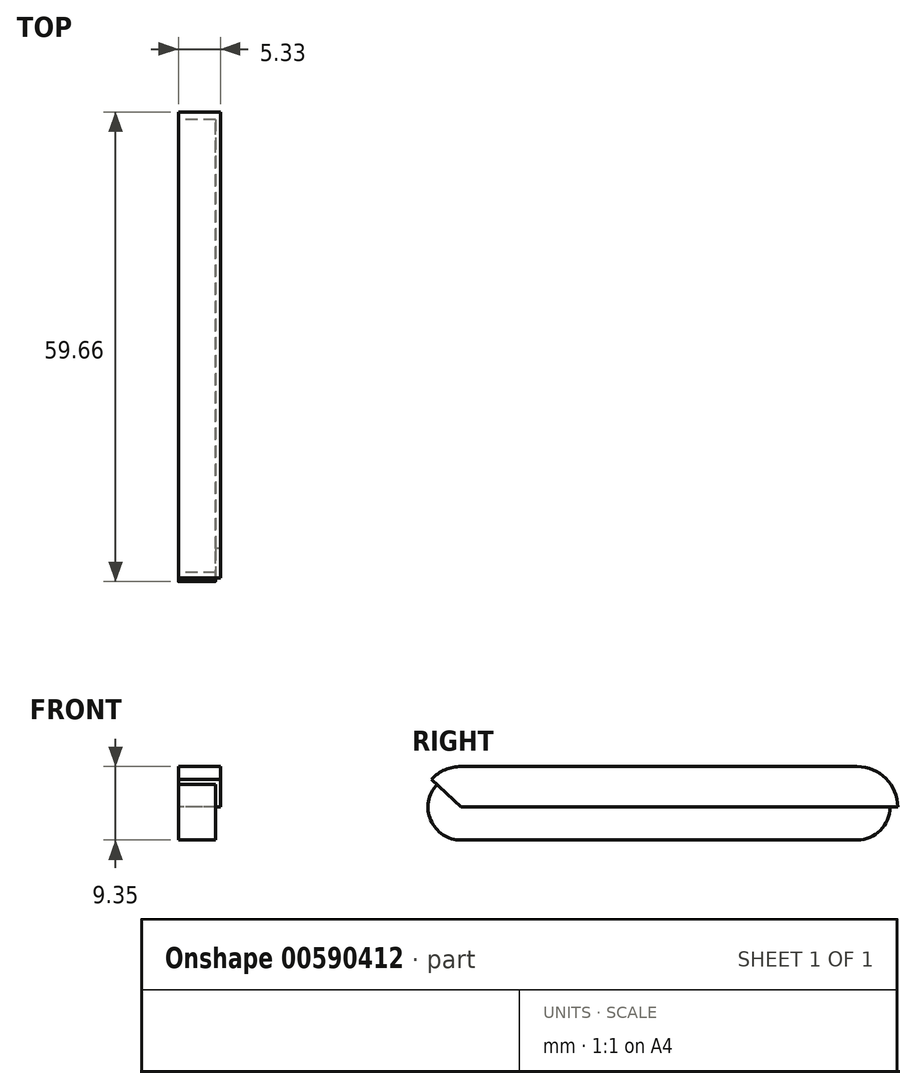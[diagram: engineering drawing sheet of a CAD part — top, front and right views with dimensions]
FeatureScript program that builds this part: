
annotation { "Feature Type Name" : "Feature", "Feature Type Description" : "" }
export const myFeature = defineFeature(function(context is Context, id is Id, definition is map)
    precondition{}
    {
        {
            var Q0;
            Q0=qCreatedBy(makeId("Right.planeOp"),FACE);
            var sketch = newSketch(context, id + "F0", { "sketchPlane" : qUnion([Q0])});
            skLineSegment(sketch, "E0", {"start": v(0, 0) * mm, "end": v(-50.32, 0) * mm});
            skLineSegment(sketch, "E1", {"start": v(0, 0) * mm, "end": v(0, 5.16) * mm});
            skLineSegment(sketch, "E2", {"start": v(0, 5.16) * mm, "end": v(-50.32, 5.16) * mm});
            skLineSegment(sketch, "E3", {"start": v(-50.32, 5.16) * mm, "end": v(-50.32, 0) * mm});
            skArc(sketch, "E4", {"start": v(0, 5.16) * mm, "mid": v(3.65, 3.65) * mm, "end": v(5.16, 0) * mm});
            skLineSegment(sketch, "E5", {"start": v(5.16, 0) * mm, "end": v(0, 0) * mm});
            skArc(sketch, "E6", {"start": v(-50.32, 5.16) * mm, "mid": v(-52.35, 4.74) * mm, "end": v(-54.06, 3.55) * mm});
            skLineSegment(sketch, "E7", {"start": v(-54.06, 3.55) * mm, "end": v(-50.32, 0) * mm});
            skSolve(sketch);
        }
        {
            var Q0;
            Q0=makeQuery(id+"F0.imprint","IMPRINT",FACE,{"disambiguationData":[TD([[makeQuery(id+"F0.imprint","IMPRINT",EDGE,{"derivedFrom":sQuery(id+"F0.wireOp",EDGE,"E0")}),-1.0]])]});
            var Q1;
            Q1=makeQuery(id+"F0.imprint","IMPRINT",FACE,{"disambiguationData":[TD([[makeQuery(id+"F0.imprint","IMPRINT",EDGE,{"derivedFrom":sQuery(id+"F0.wireOp",EDGE,"E3")}),-1.0]])]});
            var Q2;
            Q2=makeQuery(id+"F0.imprint","IMPRINT",FACE,{"disambiguationData":[TD([[makeQuery(id+"F0.imprint","IMPRINT",EDGE,{"derivedFrom":sQuery(id+"F0.wireOp",EDGE,"E1")}),-1.0]])]});
            var Q3;
            Q3=sQuery(id+"F0.wireOp",EDGE,"E2");
            var Q4;
            Q4=sQuery(id+"F0.wireOp",EDGE,"E6");
            var Q5;
            Q5=sQuery(id+"F0.wireOp",EDGE,"E7");
            var Q6;
            Q6=sQuery(id+"F0.wireOp",EDGE,"E0");
            var Q7;
            Q7=sQuery(id+"F0.wireOp",EDGE,"E4");
            var Q8;
            Q8=sQuery(id+"F0.wireOp",EDGE,"E5");
            extrude(context, id + "F1", {"entities" : qUnion([Q0, Q1, Q2]), "surfaceEntities" : qUnion([Q3, Q4, Q5, Q6, Q7, Q8]), "depth" : 5.33 * mm, "offsetDistance" : 25.4 * mm});
        }
        {
            var Q0;
            Q0=qCreatedBy(makeId("Right.planeOp"),FACE);
            var sketch = newSketch(context, id + "F2", { "sketchPlane" : qUnion([Q0])});
            skLineSegment(sketch, "E8", {"start": v(0, 0) * mm, "end": v(0, -4.19) * mm});
            skLineSegment(sketch, "E9", {"start": v(0, 0) * mm, "end": v(-50.32, 0) * mm});
            skLineSegment(sketch, "E10", {"start": v(-50.32, 0) * mm, "end": v(-50.32, -4.19) * mm});
            skLineSegment(sketch, "E11", {"start": v(-50.32, -4.19) * mm, "end": v(0, -4.19) * mm});
            skArc(sketch, "E12", {"start": v(-50.32, -4.19) * mm, "mid": v(-54.17, -1.65) * mm, "end": v(-53.35, 2.89) * mm});
            skLineSegment(sketch, "E13", {"start": v(-53.35, 2.89) * mm, "end": v(-50.32, 0) * mm});
            skArc(sketch, "E14", {"start": v(0, -4.19) * mm, "mid": v(2.96, -2.96) * mm, "end": v(4.19, 0) * mm});
            skLineSegment(sketch, "E15", {"start": v(4.19, 0) * mm, "end": v(0, 0) * mm});
            skSolve(sketch);
        }
        {
            var Q0;
            Q0=makeQuery(id+"F2.imprint","IMPRINT",FACE,{"disambiguationData":[TD([[makeQuery(id+"F2.imprint","IMPRINT",EDGE,{"derivedFrom":sQuery(id+"F2.wireOp",EDGE,"E10")}),-1.0]])]});
            var Q1;
            Q1=makeQuery(id+"F2.imprint","IMPRINT",FACE,{"disambiguationData":[TD([[makeQuery(id+"F2.imprint","IMPRINT",EDGE,{"derivedFrom":sQuery(id+"F2.wireOp",EDGE,"E8")}),-1.0]])]});
            var Q2;
            Q2=makeQuery(id+"F2.imprint","IMPRINT",FACE,{"disambiguationData":[TD([[makeQuery(id+"F2.imprint","IMPRINT",EDGE,{"derivedFrom":sQuery(id+"F2.wireOp",EDGE,"E8")}),1.0]])]});
            extrude(context, id + "F3", {"entities" : qUnion([Q0, Q1, Q2]), "operationType" : NewBodyOperationType.ADD, "depth" : 4.7 * mm, "offsetDistance" : 25.4 * mm});
        }
    });
